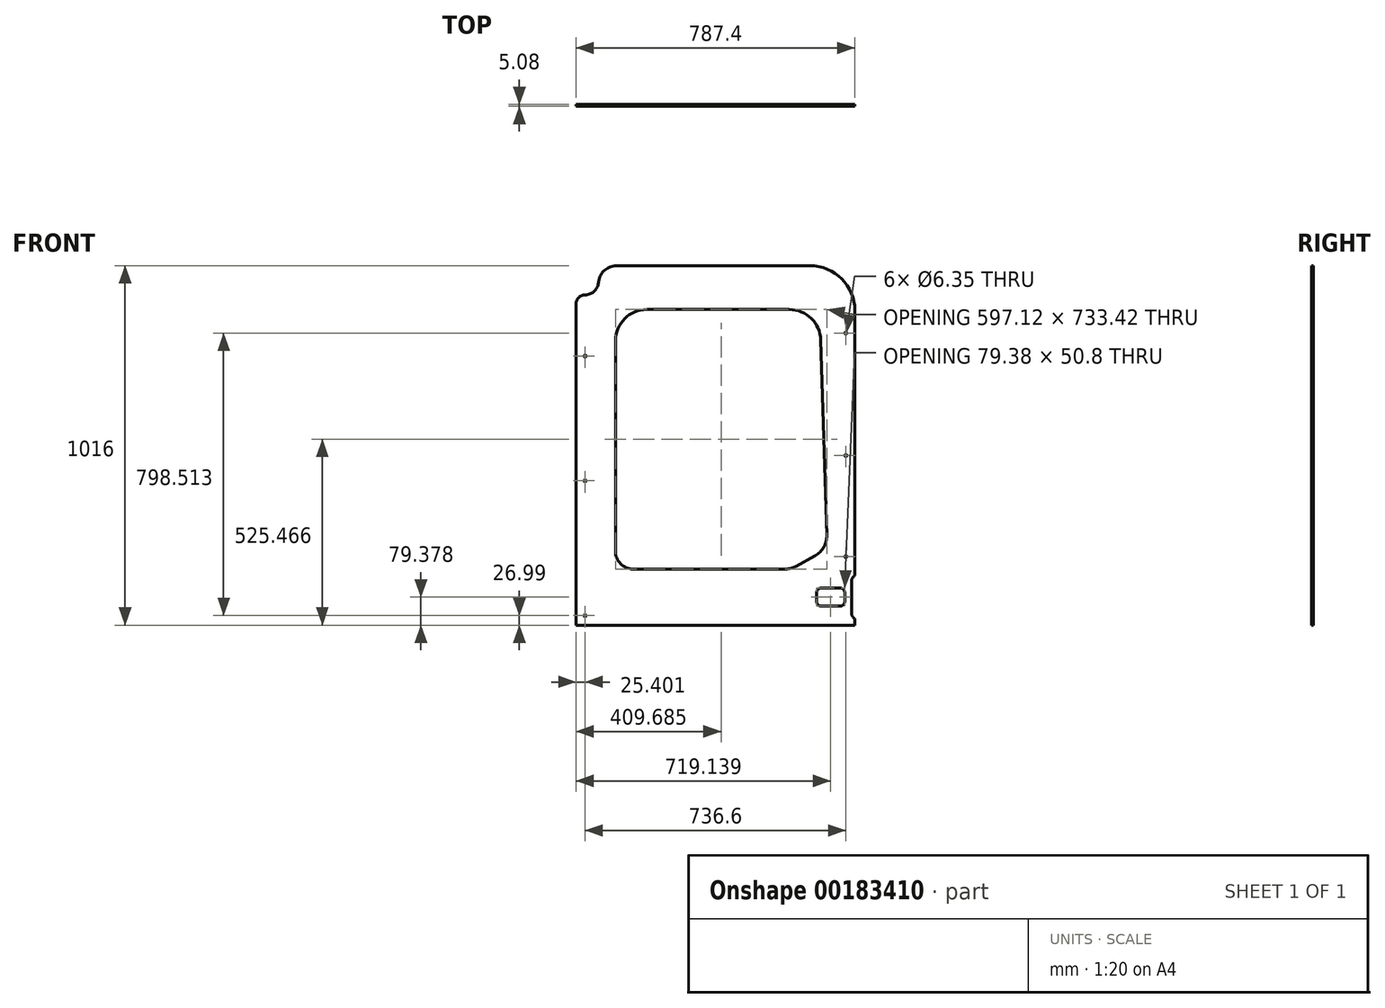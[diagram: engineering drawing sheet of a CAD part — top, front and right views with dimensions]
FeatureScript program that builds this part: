
annotation { "Feature Type Name" : "Feature", "Feature Type Description" : "" }
export const myFeature = defineFeature(function(context is Context, id is Id, definition is map)
    precondition{}
    {
        {
            var Q0;
            Q0=qCreatedBy(makeId("Front.planeOp"),FACE);
            var sketch = newSketch(context, id + "F0", { "sketchPlane" : qUnion([Q0])});
            skLineSegment(sketch, "E0.bottom", {"start": v(-393.54, 668) * mm, "end": v(393.86, 668) * mm});
            skLineSegment(sketch, "E0.top", {"start": v(-393.54, -348) * mm, "end": v(393.86, -348) * mm});
            skLineSegment(sketch, "E0.left", {"start": v(-393.54, 668) * mm, "end": v(-393.54, -348) * mm});
            skLineSegment(sketch, "E0.right", {"start": v(393.86, 668) * mm, "end": v(393.86, -348) * mm});
            skSolve(sketch);
        }
        {
            var Q0;
            Q0 = qSketchRegion(id + "F0", true);
            extrude(context, id + "F1", {"entities" : qUnion([Q0]), "depth" : 5.08 * mm});
        }
        {
            var Q0;
            Q0=makeQuery(id+"F1.opExtrude","CAP_FACE",FACE,{"disambiguationData":[OSD([sQuery(id+"F0.wireOp",EDGE,"E0.bottom"),sQuery(id+"F0.wireOp",EDGE,"E0.top"),sQuery(id+"F0.wireOp",EDGE,"E0.left"),sQuery(id+"F0.wireOp",EDGE,"E0.right")])],"isStart":false});
            var sketch = newSketch(context, id + "F2", { "sketchPlane" : qUnion([Q0])});
            skLineSegment(sketch, "E1.bottom", {"start": v(298.61, -243.23) * mm, "end": v(352.59, -243.23) * mm});
            skLineSegment(sketch, "E1.top", {"start": v(298.61, -294.03) * mm, "end": v(352.59, -294.03) * mm});
            skLineSegment(sketch, "E1.left", {"start": v(285.91, -255.93) * mm, "end": v(285.91, -281.33) * mm});
            skLineSegment(sketch, "E1.right", {"start": v(365.29, -255.93) * mm, "end": v(365.29, -281.33) * mm});
            skPoint(sketch, "E2.visualSharp", {"position": v(285.91, -243.23) * mm});
            skArc(sketch, "E2.filletArc", {"start": v(298.61, -243.23) * mm, "mid": v(289.63, -246.95) * mm, "end": v(285.91, -255.93) * mm});
            skPoint(sketch, "E3.visualSharp", {"position": v(365.29, -243.23) * mm});
            skArc(sketch, "E3.filletArc", {"start": v(365.29, -255.93) * mm, "mid": v(361.57, -246.95) * mm, "end": v(352.59, -243.23) * mm});
            skPoint(sketch, "E4.visualSharp", {"position": v(365.29, -294.03) * mm});
            skArc(sketch, "E4.filletArc", {"start": v(352.59, -294.03) * mm, "mid": v(361.57, -290.31) * mm, "end": v(365.29, -281.33) * mm});
            skPoint(sketch, "E5.visualSharp", {"position": v(285.91, -294.03) * mm});
            skArc(sketch, "E5.filletArc", {"start": v(285.91, -281.33) * mm, "mid": v(289.63, -290.31) * mm, "end": v(298.61, -294.03) * mm});
            skSolve(sketch);
        }
        {
            var Q0;
            Q0 = qSketchRegion(id + "F2", true);
            extrude(context, id + "F3", {"entities" : qUnion([Q0]), "operationType" : NewBodyOperationType.REMOVE, "endBound" : BoundingType.THROUGH_ALL, "oppositeDirection" : true, "depth" : 25.4 * mm});
        }
        {
            var Q0;
            Q0=makeQuery(id+"F1.opExtrude","CAP_FACE",FACE,{"disambiguationData":[OSD([sQuery(id+"F0.wireOp",EDGE,"E0.bottom"),sQuery(id+"F0.wireOp",EDGE,"E0.top"),sQuery(id+"F0.wireOp",EDGE,"E0.left"),sQuery(id+"F0.wireOp",EDGE,"E0.right")])],"isStart":false});
            var sketch = newSketch(context, id + "F4", { "sketchPlane" : qUnion([Q0])});
            skLineSegment(sketch, "E6.bottom", {"start": v(403.39, -205.13) * mm, "end": v(403.39, -205.13) * mm});
            skLineSegment(sketch, "E6.top", {"start": v(403.39, -332.13) * mm, "end": v(403.39, -332.13) * mm});
            skLineSegment(sketch, "E6.left", {"start": v(384.34, -224.18) * mm, "end": v(384.34, -313.08) * mm});
            skLineSegment(sketch, "E6.right", {"start": v(403.39, -205.13) * mm, "end": v(403.39, -332.13) * mm});
            skPoint(sketch, "E7.visualSharp", {"position": v(384.34, -205.13) * mm});
            skArc(sketch, "E7.filletArc", {"start": v(403.39, -205.13) * mm, "mid": v(389.92, -210.71) * mm, "end": v(384.34, -224.18) * mm});
            skPoint(sketch, "E8.visualSharp", {"position": v(384.34, -332.13) * mm});
            skArc(sketch, "E8.filletArc", {"start": v(384.34, -313.08) * mm, "mid": v(389.92, -326.55) * mm, "end": v(403.39, -332.13) * mm});
            skSolve(sketch);
        }
        {
            var Q0;
            Q0 = qSketchRegion(id + "F4", true);
            extrude(context, id + "F5", {"entities" : qUnion([Q0]), "operationType" : NewBodyOperationType.REMOVE, "endBound" : BoundingType.THROUGH_ALL, "oppositeDirection" : true, "depth" : 25.4 * mm});
        }
        {
            var Q0;
            Q0=makeQuery(id+"F1.opExtrude","CAP_FACE",FACE,{"disambiguationData":[OSD([sQuery(id+"F0.wireOp",EDGE,"E0.bottom"),sQuery(id+"F0.wireOp",EDGE,"E0.top"),sQuery(id+"F0.wireOp",EDGE,"E0.left"),sQuery(id+"F0.wireOp",EDGE,"E0.right")])],"isStart":false});
            var sketch = newSketch(context, id + "F6", { "sketchPlane" : qUnion([Q0])});
            skLineSegment(sketch, "E9.bottom", {"start": v(-193.51, 544.17) * mm, "end": v(208.7, 544.17) * mm});
            skLineSegment(sketch, "E9.top", {"start": v(-231.61, -189.26) * mm, "end": v(196.7, -189.26) * mm});
            skLineSegment(sketch, "E9.left", {"start": v(-282.41, 455.27) * mm, "end": v(-282.41, -138.46) * mm});
            skPoint(sketch, "E10.visualSharp", {"position": v(-282.41, 544.17) * mm});
            skArc(sketch, "E10.filletArc", {"start": v(-193.51, 544.17) * mm, "mid": v(-256.38, 518.13) * mm, "end": v(-282.41, 455.27) * mm});
            skLineSegment(sketch, "E11", {"start": v(297.56, 458.03) * mm, "end": v(314.7, -94.04) * mm});
            skPoint(sketch, "E12.visualSharp", {"position": v(-282.41, -189.26) * mm});
            skArc(sketch, "E12.filletArc", {"start": v(-282.41, -138.46) * mm, "mid": v(-267.53, -174.38) * mm, "end": v(-231.61, -189.26) * mm});
            skLineSegment(sketch, "E13", {"start": v(227.1, -181.5) * mm, "end": v(281.64, -151.75) * mm});
            skPoint(sketch, "E14.orphan", {"position": v(317.66, -189.26) * mm});
            skPoint(sketch, "E15.visualSharp", {"position": v(212.89, -189.26) * mm});
            skArc(sketch, "E15.filletArc", {"start": v(196.7, -189.26) * mm, "mid": v(212.38, -187.29) * mm, "end": v(227.1, -181.5) * mm});
            skPoint(sketch, "E16.newPointA", {"position": v(317.66, -132.1) * mm});
            skArc(sketch, "E16.filletArc", {"start": v(281.64, -151.75) * mm, "mid": v(306.33, -127.57) * mm, "end": v(314.7, -94.04) * mm});
            skPoint(sketch, "E17.visualSharp", {"position": v(294.88, 544.17) * mm});
            skArc(sketch, "E17.filletArc", {"start": v(297.56, 458.03) * mm, "mid": v(270.58, 519.1) * mm, "end": v(208.7, 544.17) * mm});
            skSolve(sketch);
        }
        {
            var Q0;
            Q0 = qSketchRegion(id + "F6", true);
            extrude(context, id + "F7", {"entities" : qUnion([Q0]), "operationType" : NewBodyOperationType.REMOVE, "endBound" : BoundingType.THROUGH_ALL, "oppositeDirection" : true, "depth" : 25.4 * mm});
        }
        {
            var Q0;
            Q0=makeQuery(id+"F1.opExtrude","CAP_FACE",FACE,{"disambiguationData":[OSD([sQuery(id+"F0.wireOp",EDGE,"E0.bottom"),sQuery(id+"F0.wireOp",EDGE,"E0.top"),sQuery(id+"F0.wireOp",EDGE,"E0.left"),sQuery(id+"F0.wireOp",EDGE,"E0.right")])],"isStart":false});
            var sketch = newSketch(context, id + "F8", { "sketchPlane" : qUnion([Q0])});
            skLineSegment(sketch, "E18.bottom", {"start": v(-393.54, 668) * mm, "end": v(-330.04, 668) * mm});
            skLineSegment(sketch, "E18.top", {"start": v(-393.54, 585.44) * mm, "end": v(-368.14, 585.44) * mm});
            skLineSegment(sketch, "E18.left", {"start": v(-393.54, 668) * mm, "end": v(-393.54, 585.44) * mm});
            skLineSegment(sketch, "E18.right", {"start": v(-330.04, 668) * mm, "end": v(-330.04, 623.54) * mm});
            skPoint(sketch, "E19.visualSharp", {"position": v(-330.04, 585.44) * mm});
            skArc(sketch, "E19.filletArc", {"start": v(-368.14, 585.44) * mm, "mid": v(-341.2, 596.6) * mm, "end": v(-330.04, 623.54) * mm});
            skSolve(sketch);
        }
        {
            var Q0;
            Q0 = qSketchRegion(id + "F8", true);
            extrude(context, id + "F9", {"entities" : qUnion([Q0]), "operationType" : NewBodyOperationType.REMOVE, "endBound" : BoundingType.THROUGH_ALL, "oppositeDirection" : true, "depth" : 25.4 * mm});
        }
        {
            var Q0;
            Q0=makeQuery(id+"F1.opExtrude","CAP_FACE",FACE,{"disambiguationData":[OSD([sQuery(id+"F0.wireOp",EDGE,"E0.bottom"),sQuery(id+"F0.wireOp",EDGE,"E0.top"),sQuery(id+"F0.wireOp",EDGE,"E0.left"),sQuery(id+"F0.wireOp",EDGE,"E0.right")])],"isStart":false});
            var sketch = newSketch(context, id + "F10", { "sketchPlane" : qUnion([Q0])});
            skPoint(sketch, "E20.visualSharp", {"position": v(-330.04, 668) * mm});
            skArc(sketch, "E20.filletArc", {"start": v(-279.24, 668) * mm, "mid": v(-315.16, 653.11) * mm, "end": v(-330.04, 617.2) * mm});
            skLineSegment(sketch, "E21", {"start": v(-279.24, 668) * mm, "end": v(-330.04, 668) * mm});
            skLineSegment(sketch, "E22", {"start": v(-330.04, 617.2) * mm, "end": v(-330.04, 668) * mm});
            skSolve(sketch);
        }
        {
            var Q0;
            Q0 = qSketchRegion(id + "F10", true);
            extrude(context, id + "F11", {"entities" : qUnion([Q0]), "operationType" : NewBodyOperationType.REMOVE, "endBound" : BoundingType.THROUGH_ALL, "oppositeDirection" : true, "depth" : 25.4 * mm});
        }
        {
            var Q0;
            Q0 = qSketchRegion(id + "F10", true);
            extrude(context, id + "F12", {"entities" : qUnion([Q0]), "operationType" : NewBodyOperationType.REMOVE, "oppositeDirection" : true, "depth" : 25.4 * mm});
        }
        {
            var Q0;
            Q0=makeQuery(id+"F1.opExtrude","CAP_FACE",FACE,{"disambiguationData":[OSD([sQuery(id+"F0.wireOp",EDGE,"E0.bottom"),sQuery(id+"F0.wireOp",EDGE,"E0.top"),sQuery(id+"F0.wireOp",EDGE,"E0.left"),sQuery(id+"F0.wireOp",EDGE,"E0.right")])],"isStart":false});
            var sketch = newSketch(context, id + "F13", { "sketchPlane" : qUnion([Q0])});
            skPoint(sketch, "E23.visualSharp", {"position": v(-393.54, 585.44) * mm});
            skArc(sketch, "E23.filletArc", {"start": v(-368.14, 585.44) * mm, "mid": v(-386.1, 578) * mm, "end": v(-393.54, 560.04) * mm});
            skPoint(sketch, "E24.start.orphan", {"position": v(-312.97, 579.1) * mm});
            skLineSegment(sketch, "E25", {"start": v(-368.14, 585.44) * mm, "end": v(-393.54, 585.44) * mm});
            skLineSegment(sketch, "E26", {"start": v(-393.54, 585.44) * mm, "end": v(-393.54, 560.04) * mm});
            skSolve(sketch);
        }
        {
            var Q0;
            Q0 = qSketchRegion(id + "F13", true);
            extrude(context, id + "F14", {"entities" : qUnion([Q0]), "operationType" : NewBodyOperationType.REMOVE, "endBound" : BoundingType.THROUGH_ALL, "oppositeDirection" : true, "depth" : 25.4 * mm});
        }
        {
            var Q0;
            Q0=makeQuery(id+"F1.opExtrude","CAP_FACE",FACE,{"disambiguationData":[OSD([sQuery(id+"F0.wireOp",EDGE,"E0.bottom"),sQuery(id+"F0.wireOp",EDGE,"E0.top"),sQuery(id+"F0.wireOp",EDGE,"E0.left"),sQuery(id+"F0.wireOp",EDGE,"E0.right")])],"isStart":false});
            var sketch = newSketch(context, id + "F15", { "sketchPlane" : qUnion([Q0])});
            skPoint(sketch, "E27.visualSharp", {"position": v(393.86, 668) * mm});
            skArc(sketch, "E27.filletArc", {"start": v(393.86, 541) * mm, "mid": v(356.66, 630.8) * mm, "end": v(266.86, 668) * mm});
            skLineSegment(sketch, "E28", {"start": v(266.86, 668) * mm, "end": v(393.86, 668) * mm});
            skLineSegment(sketch, "E29", {"start": v(393.86, 668) * mm, "end": v(393.86, 541) * mm});
            skSolve(sketch);
        }
        {
            var Q0;
            Q0 = qSketchRegion(id + "F15", true);
            extrude(context, id + "F16", {"entities" : qUnion([Q0]), "operationType" : NewBodyOperationType.REMOVE, "endBound" : BoundingType.THROUGH_ALL, "oppositeDirection" : true, "depth" : 25.4 * mm});
        }
        {
            var Q0;
            Q0=makeQuery(id+"F1.opExtrude","CAP_FACE",FACE,{"disambiguationData":[OSD([sQuery(id+"F0.wireOp",EDGE,"E0.bottom"),sQuery(id+"F0.wireOp",EDGE,"E0.top"),sQuery(id+"F0.wireOp",EDGE,"E0.left"),sQuery(id+"F0.wireOp",EDGE,"E0.right")])],"isStart":false});
            var sketch = newSketch(context, id + "F17", { "sketchPlane" : qUnion([Q0])});
            skCircle(sketch, "E30", {"center": v(368.46, 477.5) * mm, "radius": 3.18 * mm});
            skPoint(sketch, "E30.first.point", {"position": v(367.38, 480.48) * mm});
            skPoint(sketch, "E30.second.point", {"position": v(366.64, 474.9) * mm});
            skPoint(sketch, "E30.third.point", {"position": v(365.33, 476.94) * mm});
            skCircle(sketch, "E31", {"center": v(368.46, 131.42) * mm, "radius": 3.18 * mm});
            skPoint(sketch, "E31.first.point", {"position": v(367.03, 134.25) * mm});
            skPoint(sketch, "E31.second.point", {"position": v(369.19, 128.33) * mm});
            skPoint(sketch, "E31.third.point", {"position": v(371.61, 131.02) * mm});
            skCircle(sketch, "E32", {"center": v(368.46, -154.33) * mm, "radius": 3.18 * mm});
            skPoint(sketch, "E32.first.point", {"position": v(367.13, -151.45) * mm});
            skPoint(sketch, "E32.second.point", {"position": v(367.23, -151.4) * mm});
            skCircle(sketch, "E33", {"center": v(-368.14, -321.02) * mm, "radius": 3.18 * mm});
            skPoint(sketch, "E33.first.point", {"position": v(-369.44, -323.91) * mm});
            skPoint(sketch, "E33.second.point", {"position": v(-365.62, -322.96) * mm});
            skPoint(sketch, "E33.third.point", {"position": v(-368.49, -317.86) * mm});
            skCircle(sketch, "E34", {"center": v(-368.14, 59.98) * mm, "radius": 3.17 * mm});
            skPoint(sketch, "E34.first.point", {"position": v(-371.31, 60.12) * mm});
            skPoint(sketch, "E34.second.point", {"position": v(-365.4, 58.37) * mm});
            skPoint(sketch, "E34.third.point", {"position": v(-365.4, 58.37) * mm});
            skCircle(sketch, "E35", {"center": v(-368.14, 412.4) * mm, "radius": 3.18 * mm});
            skPoint(sketch, "E35.first.point", {"position": v(-369.15, 415.42) * mm});
            skPoint(sketch, "E35.second.point", {"position": v(-366.5, 409.68) * mm});
            skPoint(sketch, "E35.third.point", {"position": v(-366.94, 409.46) * mm});
            skSolve(sketch);
        }
        {
            var Q0;
            Q0 = qSketchRegion(id + "F17", true);
            extrude(context, id + "F18", {"entities" : qUnion([Q0]), "operationType" : NewBodyOperationType.REMOVE, "endBound" : BoundingType.THROUGH_ALL, "oppositeDirection" : true, "depth" : 25.4 * mm});
        }
    });
